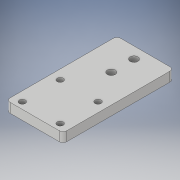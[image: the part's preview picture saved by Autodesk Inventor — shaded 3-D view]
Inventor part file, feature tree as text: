
AUTODESK INVENTOR PART (.ipt)
format: ipt  version: 2018 (Build 220112000, 112)  size: 181,760 bytes
history: native  units: in
note: dims shown in document units (in); Inventor stores cm internally (conversion verified against a paired STEP export)
features: extrude x7, sketch x7, mirror x1, fillet x1
ambient origin geometry x8: Origin, YZ Plane, XZ Plane, XY Plane, X Axis, Y Axis, Z Axis, Center Point
bodies: Solid1 (feature_tree)
feature tree (16):
  extrude  "Extrusion1"  Depth=2.3031in
  extrude  "Extrusion2"  Depth=0.1969in
  extrude  "Extrusion3"  Depth=0.7874in
  extrude  "Extrusion4"  Depth=0.1969in TaperAngle=0.0deg
  extrude  "Extrusion5"  Depth=0.9843in
  mirror  "Mirror1"
  extrude  "Extrusion6"  Depth=0.2362in
  fillet  "Fillet1"  Radius=0.4724in
  extrude  "Extrusion7"  Depth=0.1969in
  sketch  "Sketch1"  dims[d0=1.1811in d1=2.3031in]
  sketch  "Sketch2"  dims[d2=0.1969in d3=0.0in d4=0.126in]
  sketch  "Sketch3"  dims[d5=0.7874in d6=0.7874in]
  sketch  "Sketch4"  dims[d7=0.1378in d8=0.1969in d9=0.0in]
  sketch  "Sketch5"  dims[d10=0.7874in d11=0.9843in]
  sketch  "Sketch6"  dims[d12=0.1654in d13=0.2362in d14=0.4724in]
  sketch  "Sketch7"  dims[d15=0.1969in d16=0.0in d17=0.1969in d18=0.7874in d19=0.7087in d20=0.1969in d21=0.0in d25=0.1969in d26=0.0in d27=0.1969in d28=0.0in d29=0.1654in d30=0.0787in d31=0.1969in d32=0.0in]
